# Revit family: rba-bim-B3949
name_source: partatom
category: Plumbing Fixtures
revit_build: Autodesk Revit 2018 (Build: 20170223_1515(x64)
units: mm (PartAtom-declared; Revit-internal decimal feet)

## family parameters
Cut with Voids When Loaded = No
Host = Face
OmniClass Number = 23.40.20.21
OmniClass Title = Toilet and Bath Specialties
Part Type = Normal
Room Calculation Point = Yes
Round Connector Dimension = Use Diameter
Shared = Yes

## types (1)
- B-3949
    Assembly Code = E1090900
    Capacity = 600 C-fold Towels  ;  800 Multifold Towels  ;  12 gal Waste
    Default Elevation = 1219 mm
    Description = Surface Mounted Convertible Combination Towel and Waste Unit
    Expected Lifespan (Years) = 0
    Installation-Fabrication = http://www.bobrick.com
    Keynote = 102813
    Maintenance Schedule (Months) = 0
    Manufacturer = Bobrick Washroom Equipment, Inc.
    Manufacturer Fax = 818-503-1930
    Manufacturer Website = http://www.bobrick.com
    Materials and Finishes = Stainless Steel Satin Finish
    Model = B3949
    Modified Issue = 20200831.01
    Product Data = http://arcat.com
    Revision = R1_10_2012
    Sales Information = http://www.bobrick.com
    Send Message = http://www.arcat.com
    URL = www.rba.com.au
    Unit Depth = 206 mm
    Unit Height = 1430 mm
    Unit Width = 445 mm
    Warranty Duration (Years) = 0

## geometry (parser evidence)
native form markers: Blend x2, Sweep x3
no freeform markers — native parametric forms only
